# Revit family: Faucet-Wall_Mount-Utility-KOHLER-Triton_Bowe-K-820T20_1
name_source: partatom
category: Plumbing Fixtures
revit_build: Autodesk Revit 2017 (Build: 20160225_1515(x64)
units: mm (PartAtom-declared; Revit-internal decimal feet)

## family parameters
Cut with Voids When Loaded = No
Host = Face
OmniClass Number = 23.31.11.00
OmniClass Title = Faucets
Part Type = Normal
Room Calculation Point = No
Round Connector Dimension = Use Diameter
Shared = No

## types (2) — shared parameters
ADA Compliant = Yes
Assembly Code = D2010
CW Connection = Yes
Cold Water Inlet = Cold Water Inlet
Date Modified = 03/31/2020
Default Elevation = 36"
Description = sink faucet
Drain Included = No
Faucet Hole Spacing = 8"
Finish = Kohler-Metal-CP-Polished_Chrome
Flow Rate = 2 GPM
HW Connection = Yes
Height = 4 5/16"
Hot Water Inlet = Hot Water Inlet
Length = 11"
Manufacturer = KOHLER Co.
MasterFormat 1995 = 15410
MasterFormat 2004 = 22.41.39
Material = Solid Brass Construction
Pressure = 60.00 psi
Product Documentation Link = https://www.us.kohler.com
Product Name = Triton Bowe
Product Page URL = http://www.us.kohler.com
Spout Reach = 11"
URL = https://www.us.kohler.com
Vent Connection = No
Waste Connection = No
Waste Water Outlet = Waste Water Outlet
WaterSense Certified = No
Width = 8"

## per-type parameters (varying)
| type | Handle Clearance | Handle Height | Lever Handle | Model | Type | Wristblade Lever Handle |
| Lever Handle , CP-Polished Chrome | 2 7/16" | 3 3/4" | Yes | K-820T20-4AFA-CP | 1 | No |
| Wristblade Lever Handle , CP-Polished Chrome | 4 1/16" | 5 1/8" | No | K-820T20-5AFA-CP | 2 | Yes |

## geometry (parser evidence)
native form markers: Sweep x5
no freeform markers — native parametric forms only
